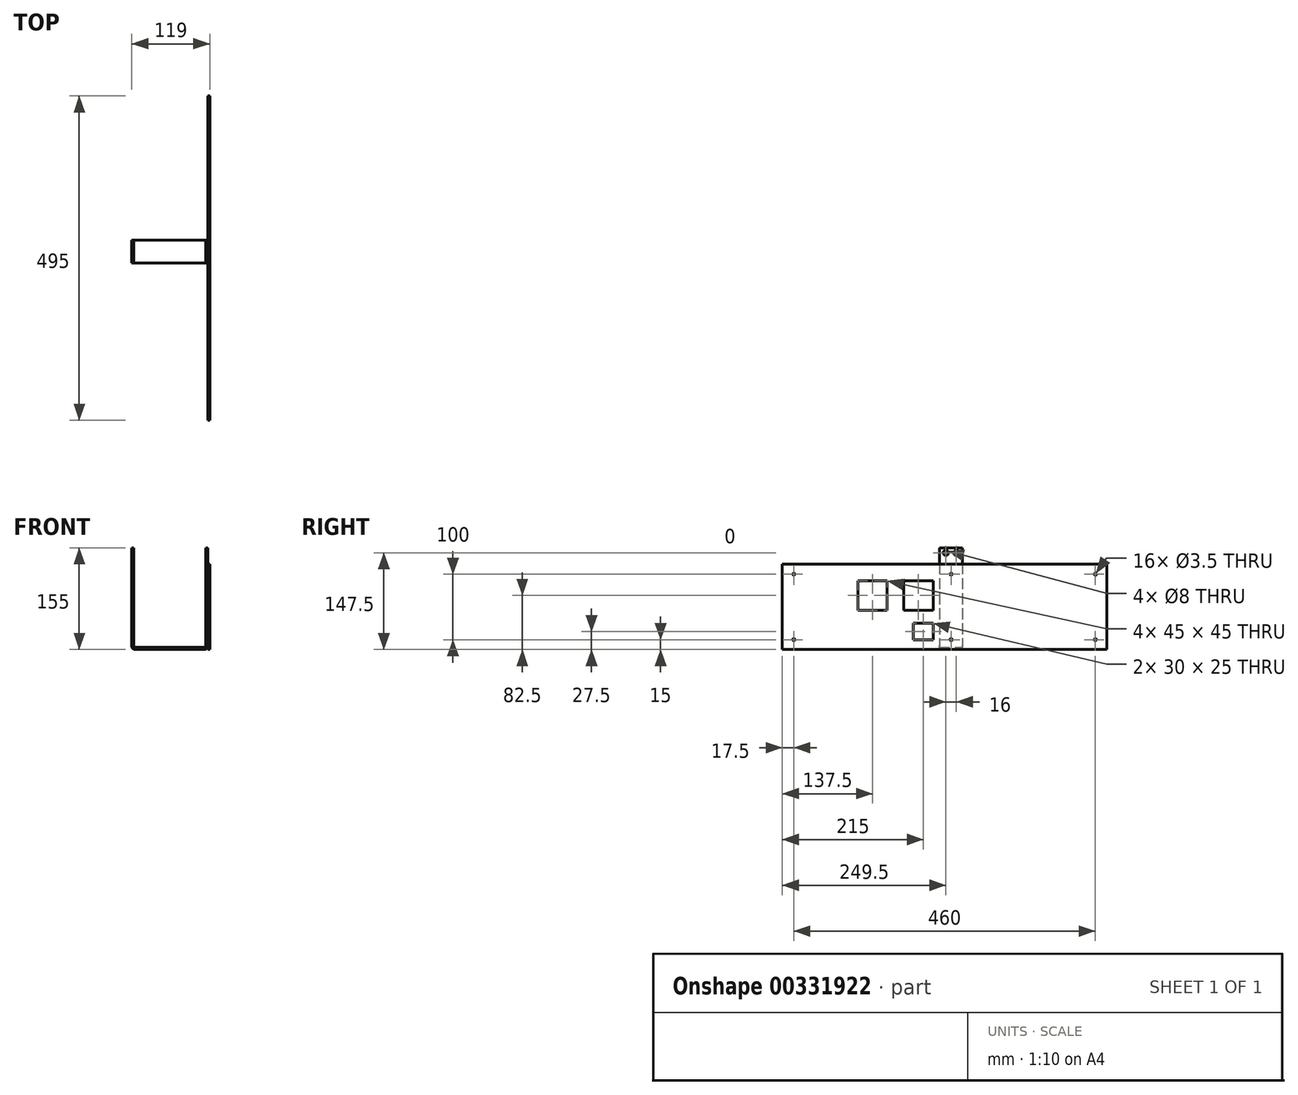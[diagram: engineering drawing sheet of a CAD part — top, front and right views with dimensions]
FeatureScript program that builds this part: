
annotation { "Feature Type Name" : "Feature", "Feature Type Description" : "" }
export const myFeature = defineFeature(function(context is Context, id is Id, definition is map)
    precondition{}
    {
        {
            var Q0;
            Q0=qCreatedBy(makeId("Front.planeOp"),FACE);
            var sketch = newSketch(context, id + "F0", { "sketchPlane" : qUnion([Q0])});
            skLineSegment(sketch, "E0.bottom", {"start": v(58, 77.5) * mm, "end": v(-58, 77.5) * mm, "construction": true});
            skLineSegment(sketch, "E0.top", {"start": v(58, -77.5) * mm, "end": v(-58, -77.5) * mm});
            skLineSegment(sketch, "E0.left", {"start": v(58, 77.5) * mm, "end": v(58, -77.5) * mm});
            skLineSegment(sketch, "E0.right", {"start": v(-58, 77.5) * mm, "end": v(-58, -77.5) * mm});
            skPoint(sketch, "E0.middle", {"position": v(0, 0) * mm});
            skLineSegment(sketch, "E1.0", {"start": v(55, 77.5) * mm, "end": v(55, -74.5) * mm});
            skLineSegment(sketch, "E1.1", {"start": v(55, -74.5) * mm, "end": v(-55, -74.5) * mm});
            skLineSegment(sketch, "E1.2", {"start": v(-55, 77.5) * mm, "end": v(-55, -74.5) * mm});
            skLineSegment(sketch, "E2", {"start": v(-58, 77.5) * mm, "end": v(-55, 77.5) * mm});
            skLineSegment(sketch, "E3", {"start": v(55, 77.5) * mm, "end": v(58, 77.5) * mm});
            skSolve(sketch);
        }
        {
            var Q0;
            Q0 = qSketchRegion(id + "F0", true);
            extrude(context, id + "F1", {"entities" : qUnion([Q0]), "depth" : 35 * mm});
        }
        {
            var Q0;
            Q0=makeQuery(id+"F1.opExtrude","SWEPT_EDGE",EDGE,{"disambiguationData":[OSD([sQuery(id+"F0.wireOp",EDGE,"E1.0"),sQuery(id+"F0.wireOp",EDGE,"E1.1")])]});
            fillet(context, id + "F2", {"entities" : qUnion([Q0]), "radius" : 3 * mm, "tangentPropagation" : true, "allowEdgeOverflow" : false});
        }
        {
            var Q0;
            Q0=makeQuery(id+"F1.opExtrude","SWEPT_EDGE",EDGE,{"disambiguationData":[OSD([sQuery(id+"F0.wireOp",EDGE,"E0.top"),sQuery(id+"F0.wireOp",EDGE,"E0.right")])]});
            var Q1;
            Q1=makeQuery(id+"F1.opExtrude","SWEPT_EDGE",EDGE,{"disambiguationData":[OSD([sQuery(id+"F0.wireOp",EDGE,"E0.top"),sQuery(id+"F0.wireOp",EDGE,"E0.left")])]});
            fillet(context, id + "F3", {"entities" : qUnion([Q0, Q1]), "radius" : 5 * mm, "tangentPropagation" : true, "allowEdgeOverflow" : false});
        }
        {
            var Q0;
            Q0=makeQuery(id+"F1.opExtrude","SWEPT_FACE",FACE,{"disambiguationData":[OSD([sQuery(id+"F0.wireOp",EDGE,"E0.right")])]});
            var sketch = newSketch(context, id + "F4", { "sketchPlane" : qUnion([Q0])});
            skCircle(sketch, "E4", {"center": v(9.5, 70) * mm, "radius": 4 * mm});
            skCircle(sketch, "E5", {"center": v(25.5, 70) * mm, "radius": 4 * mm});
            skLineSegment(sketch, "E6", {"start": v(9.5, 70) * mm, "end": v(0, 77.5) * mm, "construction": true});
            skLineSegment(sketch, "E7", {"start": v(25.5, 70) * mm, "end": v(35, 77.5) * mm, "construction": true});
            skSolve(sketch);
        }
        {
            var Q0;
            Q0 = qSketchRegion(id + "F4", true);
            extrude(context, id + "F5", {"entities" : qUnion([Q0]), "operationType" : NewBodyOperationType.REMOVE, "endBound" : BoundingType.THROUGH_ALL, "oppositeDirection" : true, "depth" : 25 * mm});
        }
        {
            var Q0;
            Q0=makeQuery(id+"F1.opExtrude","SWEPT_FACE",FACE,{"disambiguationData":[OSD([sQuery(id+"F0.wireOp",EDGE,"E0.left")])]});
            var sketch = newSketch(context, id + "F6", { "sketchPlane" : qUnion([Q0])});
            skLineSegment(sketch, "E8.bottom", {"start": v(-275, -77.5) * mm, "end": v(220, -77.5) * mm});
            skLineSegment(sketch, "E8.top", {"start": v(-275, 52.5) * mm, "end": v(220, 52.5) * mm});
            skLineSegment(sketch, "E8.left", {"start": v(-275, 52.5) * mm, "end": v(-275, -77.5) * mm});
            skLineSegment(sketch, "E8.right", {"start": v(220, 52.5) * mm, "end": v(220, -77.5) * mm});
            skPoint(sketch, "E9", {"position": v(-27.5, -77.5) * mm});
            skPoint(sketch, "E10", {"position": v(-17.5, 77.5) * mm});
            skSolve(sketch);
        }
        {
            var Q0;
            Q0 = qSketchRegion(id + "F6", true);
            extrude(context, id + "F7", {"entities" : qUnion([Q0]), "depth" : 1.5 * mm});
        }
        {
            var Q0;
            Q0=makeQuery(id+"F7.opExtrude","CAP_FACE",FACE,{"disambiguationData":[OSD([sQuery(id+"F6.wireOp",EDGE,"E8.bottom"),sQuery(id+"F6.wireOp",EDGE,"E8.top"),sQuery(id+"F6.wireOp",EDGE,"E8.left"),sQuery(id+"F6.wireOp",EDGE,"E8.right")])],"isStart":false});
            var sketch = newSketch(context, id + "F8", { "sketchPlane" : qUnion([Q0])});
            skCircle(sketch, "E11", {"center": v(-17.5, 37.5) * mm, "radius": 1.75 * mm});
            skCircle(sketch, "E12", {"center": v(-17.5, -62.5) * mm, "radius": 1.75 * mm});
            skCircle(sketch, "E13", {"center": v(202.5, -62.5) * mm, "radius": 1.75 * mm});
            skCircle(sketch, "E14", {"center": v(202.5, 37.5) * mm, "radius": 1.75 * mm});
            skCircle(sketch, "E15", {"center": v(-257.5, 37.5) * mm, "radius": 1.75 * mm});
            skCircle(sketch, "E16", {"center": v(-257.5, -62.5) * mm, "radius": 1.75 * mm});
            skLineSegment(sketch, "E17", {"start": v(-275, 52.5) * mm, "end": v(-257.5, 37.5) * mm, "construction": true});
            skLineSegment(sketch, "E18", {"start": v(202.5, 37.5) * mm, "end": v(220, 52.5) * mm, "construction": true});
            skSolve(sketch);
        }
        {
            var Q0;
            Q0 = qSketchRegion(id + "F8", true);
            extrude(context, id + "F9", {"entities" : qUnion([Q0]), "operationType" : NewBodyOperationType.REMOVE, "endBound" : BoundingType.THROUGH_ALL, "oppositeDirection" : true, "depth" : 25 * mm});
        }
        {
            var Q0;
            Q0=makeQuery(id+"F7.opExtrude","CAP_FACE",FACE,{"disambiguationData":[OSD([sQuery(id+"F6.wireOp",EDGE,"E8.bottom"),sQuery(id+"F6.wireOp",EDGE,"E8.top"),sQuery(id+"F6.wireOp",EDGE,"E8.left"),sQuery(id+"F6.wireOp",EDGE,"E8.right")])],"isStart":false});
            extrude(context, id + "F10", {"entities" : qUnion([Q0]), "depth" : 1.5 * mm});
        }
        {
            var Q0;
            Q0=makeQuery(id+"F10.opExtrude","CAP_FACE",FACE,{"disambiguationData":[OSD([sQuery(id+"F6.wireOp",EDGE,"E8.bottom"),sQuery(id+"F6.wireOp",EDGE,"E8.top"),sQuery(id+"F6.wireOp",EDGE,"E8.left"),sQuery(id+"F6.wireOp",EDGE,"E8.right")])],"isStart":false});
            var sketch = newSketch(context, id + "F11", { "sketchPlane" : qUnion([Q0])});
            skLineSegment(sketch, "E19.bottom", {"start": v(-90, -17.5) * mm, "end": v(-45, -17.5) * mm});
            skLineSegment(sketch, "E19.top", {"start": v(-90, 27.5) * mm, "end": v(-45, 27.5) * mm});
            skLineSegment(sketch, "E19.left", {"start": v(-90, -17.5) * mm, "end": v(-90, 27.5) * mm});
            skLineSegment(sketch, "E19.right", {"start": v(-45, -17.5) * mm, "end": v(-45, 27.5) * mm});
            skLineSegment(sketch, "E20.bottom", {"start": v(-160, -17.5) * mm, "end": v(-115, -17.5) * mm});
            skLineSegment(sketch, "E20.top", {"start": v(-160, 27.5) * mm, "end": v(-115, 27.5) * mm});
            skLineSegment(sketch, "E20.left", {"start": v(-160, -17.5) * mm, "end": v(-160, 27.5) * mm});
            skLineSegment(sketch, "E20.right", {"start": v(-115, -17.5) * mm, "end": v(-115, 27.5) * mm});
            skSolve(sketch);
        }
        {
            var Q0;
            Q0 = qSketchRegion(id + "F11", true);
            extrude(context, id + "F12", {"entities" : qUnion([Q0]), "operationType" : NewBodyOperationType.REMOVE, "oppositeDirection" : true, "depth" : 25 * mm});
        }
        {
            var Q0;
            Q0=makeQuery(id+"F7.opExtrude","CAP_FACE",FACE,{"disambiguationData":[OSD([sQuery(id+"F6.wireOp",EDGE,"E8.bottom"),sQuery(id+"F6.wireOp",EDGE,"E8.top"),sQuery(id+"F6.wireOp",EDGE,"E8.left"),sQuery(id+"F6.wireOp",EDGE,"E8.right")])],"isStart":true});
            var sketch = newSketch(context, id + "F13", { "sketchPlane" : qUnion([Q0])});
            skLineSegment(sketch, "E21.bottom", {"start": v(45, -62.5) * mm, "end": v(75, -62.5) * mm});
            skLineSegment(sketch, "E21.top", {"start": v(45, -37.5) * mm, "end": v(75, -37.5) * mm});
            skLineSegment(sketch, "E21.left", {"start": v(45, -62.5) * mm, "end": v(45, -37.5) * mm});
            skLineSegment(sketch, "E21.right", {"start": v(75, -62.5) * mm, "end": v(75, -37.5) * mm});
            skSolve(sketch);
        }
        {
            var Q0;
            Q0 = qSketchRegion(id + "F13", true);
            extrude(context, id + "F14", {"entities" : qUnion([Q0]), "operationType" : NewBodyOperationType.REMOVE, "oppositeDirection" : true, "depth" : 25 * mm});
        }
    });
